# Revit family: Immergas-Ares pro 230
name_source: partatom
category: Attrezzatura meccanica
revit_build: Autodesk Revit 2018 (Build: 20181015_0930(x64)
units: mm (PartAtom-declared; Revit-internal decimal feet)

## family parameters
Basato su piano di lavoro = No
Condiviso = No
Punto di calcolo locali = No
Quota connettore circolare = Usa diametro
Sempre verticale = Sì
Taglio con vuoti quando caricato = No
Tipo di parte = Normale

## types (1)
- Immergas-Ares pro 230
    Case = Immergas - Alluminio
    Diameter of fume exhaust = 250 mm  [stored 0.82021 ft]
    Dimensions of Piping Connectors = 19 mm
    ETIM Note = Residential heating
    Electric Power = 195 W
    Frequency of use = 50 Hz
    Hot water flow = 0.0 L/s
    Hydraulic Fittings = 1651 mm
    Manufacturer Product Link = https://www.immergas.com
    Mass = 479.00 kg
    MasterFormat = 23 00 00- Heating, Ventilating, and Air Conditioning (HVAC)
    Masterformat 2014 Description = Heating, Ventilating, and Air Conditioning (HVAC)
    Modello = Immergas-Ares pro 230
    Name BIM&CO = Caldaia
    Nominal Current = 6 A
    Nominal Voltage = 230 V
    Omniclass Description = HVAC Specific Products and Equipment
    Operating Temperature = 90 °C
    Overall Depth = 1082 mm  [stored 3.54987 ft]
    Overall Height = 1917 mm  [stored 6.28937 ft]
    Overall Width = 846 mm  [stored 2.77559 ft]
    Piping volume boiler = 0.21 m³
    Product Code = 3.028310
    Produttore = Immergas
    Thermal power 80/60°C = 209290 W
    UDP_334_495_PORTATA_TERMICA = 214
    UDP_88_494_GAS_CONNECTION_DIAMETER = 0.75
    Uniformat = Heat Generating Systems
    Uniformat II Description = Heat Generating Systems
    Uniformat code = D3020
    cerniere = Immergas - Plastica Nero
    yield hvac heating load nominal (%) = 97.8
    yield hvac heating load nominal 30 (%) = 96.5

note: [stored X ft] marks values corroborated as IEEE doubles in the binary element streams (Revit-internal decimal feet)
